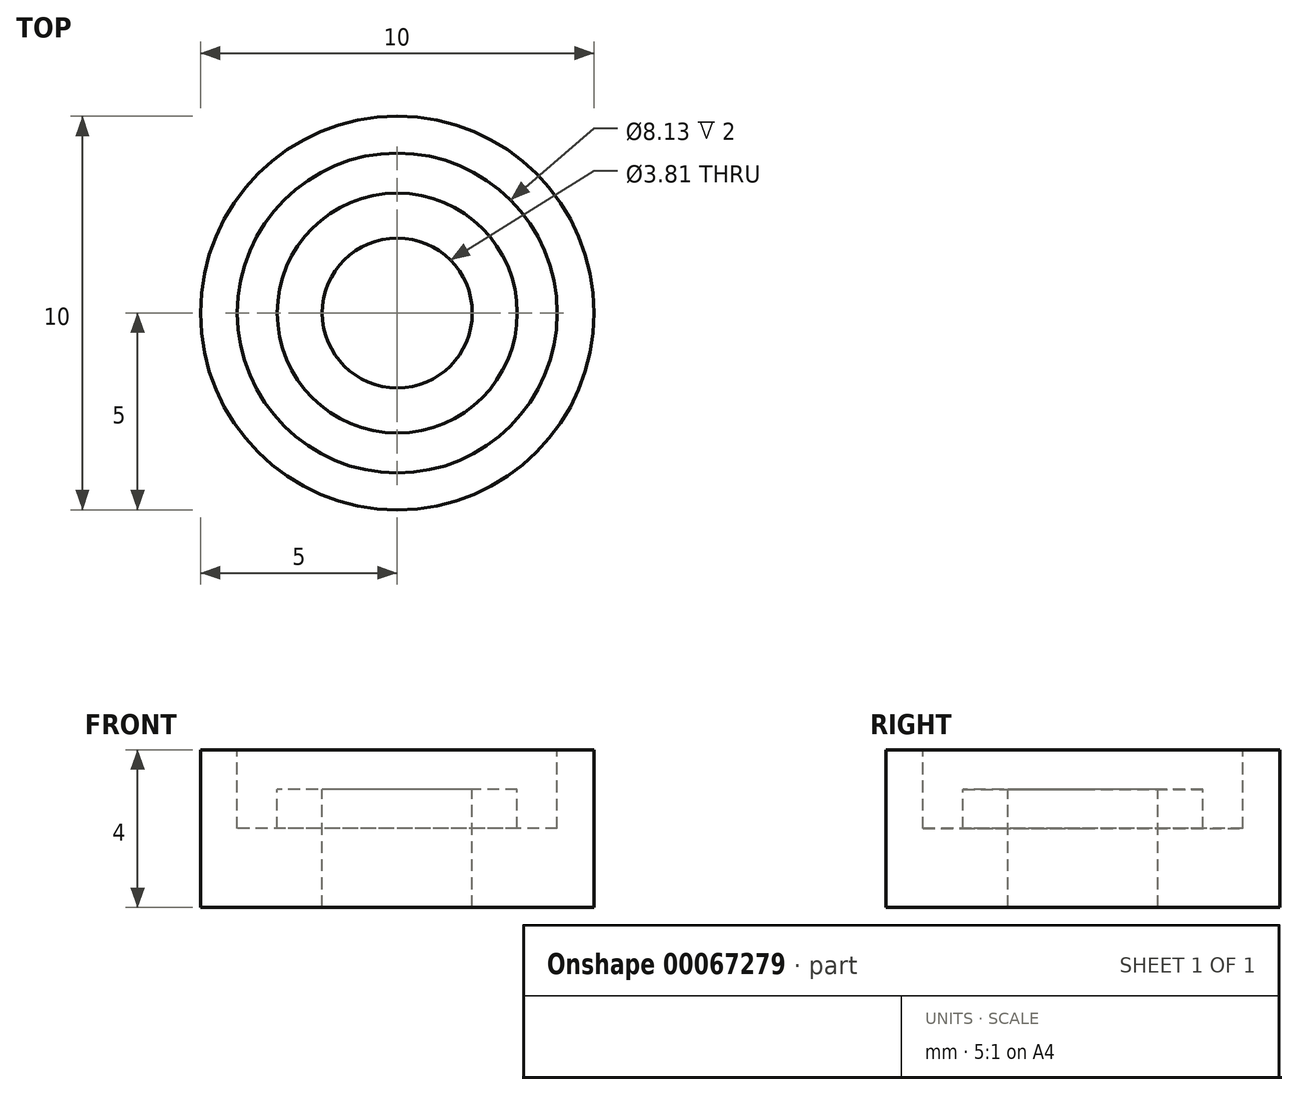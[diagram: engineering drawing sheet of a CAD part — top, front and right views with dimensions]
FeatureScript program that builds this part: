
annotation { "Feature Type Name" : "Feature", "Feature Type Description" : "" }
export const myFeature = defineFeature(function(context is Context, id is Id, definition is map)
    precondition{}
    {
        {
            var Q0;
            Q0=qCreatedBy(makeId("Top.planeOp"),FACE);
            var sketch = newSketch(context, id + "F0", { "sketchPlane" : qUnion([Q0])});
            skCircle(sketch, "E0", {"center": v(0, 0) * mm, "radius": 5 * mm});
            skSolve(sketch);
        }
        {
            var Q0;
            Q0=makeQuery(id+"F0.imprint","IMPRINT",FACE,{"disambiguationData":[TD([[makeQuery(id+"F0.imprint","IMPRINT",EDGE,{"derivedFrom":sQuery(id+"F0.wireOp",EDGE,"E0")}),1.0]])]});
            extrude(context, id + "F1", {"entities" : qUnion([Q0]), "depth" : 4 * mm});
        }
        {
            var Q0;
            Q0=makeQuery(id+"F1.opExtrude","CAP_FACE",FACE,{"disambiguationData":[OSD([sQuery(id+"F0.wireOp",EDGE,"E0")])],"isStart":false});
            var sketch = newSketch(context, id + "F2", { "sketchPlane" : qUnion([Q0])});
            skCircle(sketch, "E1", {"center": v(0, 0) * mm, "radius": 4.06 * mm});
            skCircle(sketch, "E2", {"center": v(0, 0) * mm, "radius": 3.05 * mm});
            skSolve(sketch);
        }
        {
            var Q0;
            Q0=makeQuery(id+"F2.imprint","IMPRINT",FACE,{"disambiguationData":[TD([[makeQuery(id+"F2.imprint","IMPRINT",EDGE,{"derivedFrom":sQuery(id+"F2.wireOp",EDGE,"E1")}),1.0]])]});
            extrude(context, id + "F3", {"entities" : qUnion([Q0]), "operationType" : NewBodyOperationType.REMOVE, "oppositeDirection" : true, "depth" : 2 * mm});
        }
        {
            var Q0;
            Q0=makeQuery(id+"F3.boolean.opBoolean","SPLIT",FACE,{"disambiguationData":[TD([makeQuery(id+"F3.opExtrude","SWEPT_FACE",FACE,{"disambiguationData":[OSD([sQuery(id+"F2.wireOp",EDGE,"E2")])]})])],"derivedFrom":makeQuery(id+"F1.opExtrude","CAP_FACE",FACE,{"disambiguationData":[OSD([sQuery(id+"F0.wireOp",EDGE,"E0")])],"isStart":false})});
            extrude(context, id + "F4", {"entities" : qUnion([Q0]), "operationType" : NewBodyOperationType.REMOVE, "oppositeDirection" : true, "depth" : 1 * mm});
        }
        {
            var Q0;
            Q0=makeQuery(id+"F4.boolean.opBoolean","COPY",FACE,{"derivedFrom":makeQuery(id+"F4.opExtrude","CAP_FACE",FACE,{"disambiguationData":[OSD([sQuery(id+"F0.wireOp",EDGE,"E0")])],"isStart":false})});
            var sketch = newSketch(context, id + "F5", { "sketchPlane" : qUnion([Q0])});
            skCircle(sketch, "E3", {"center": v(0, 0) * mm, "radius": 1.9 * mm});
            skSolve(sketch);
        }
        {
            var Q0;
            Q0=makeQuery(id+"F5.imprint","IMPRINT",FACE,{"disambiguationData":[TD([[makeQuery(id+"F5.imprint","IMPRINT",EDGE,{"derivedFrom":sQuery(id+"F5.wireOp",EDGE,"E3")}),1.0]])]});
            extrude(context, id + "F6", {"entities" : qUnion([Q0]), "operationType" : NewBodyOperationType.REMOVE, "oppositeDirection" : true, "depth" : 25.4 * mm});
        }
    });
